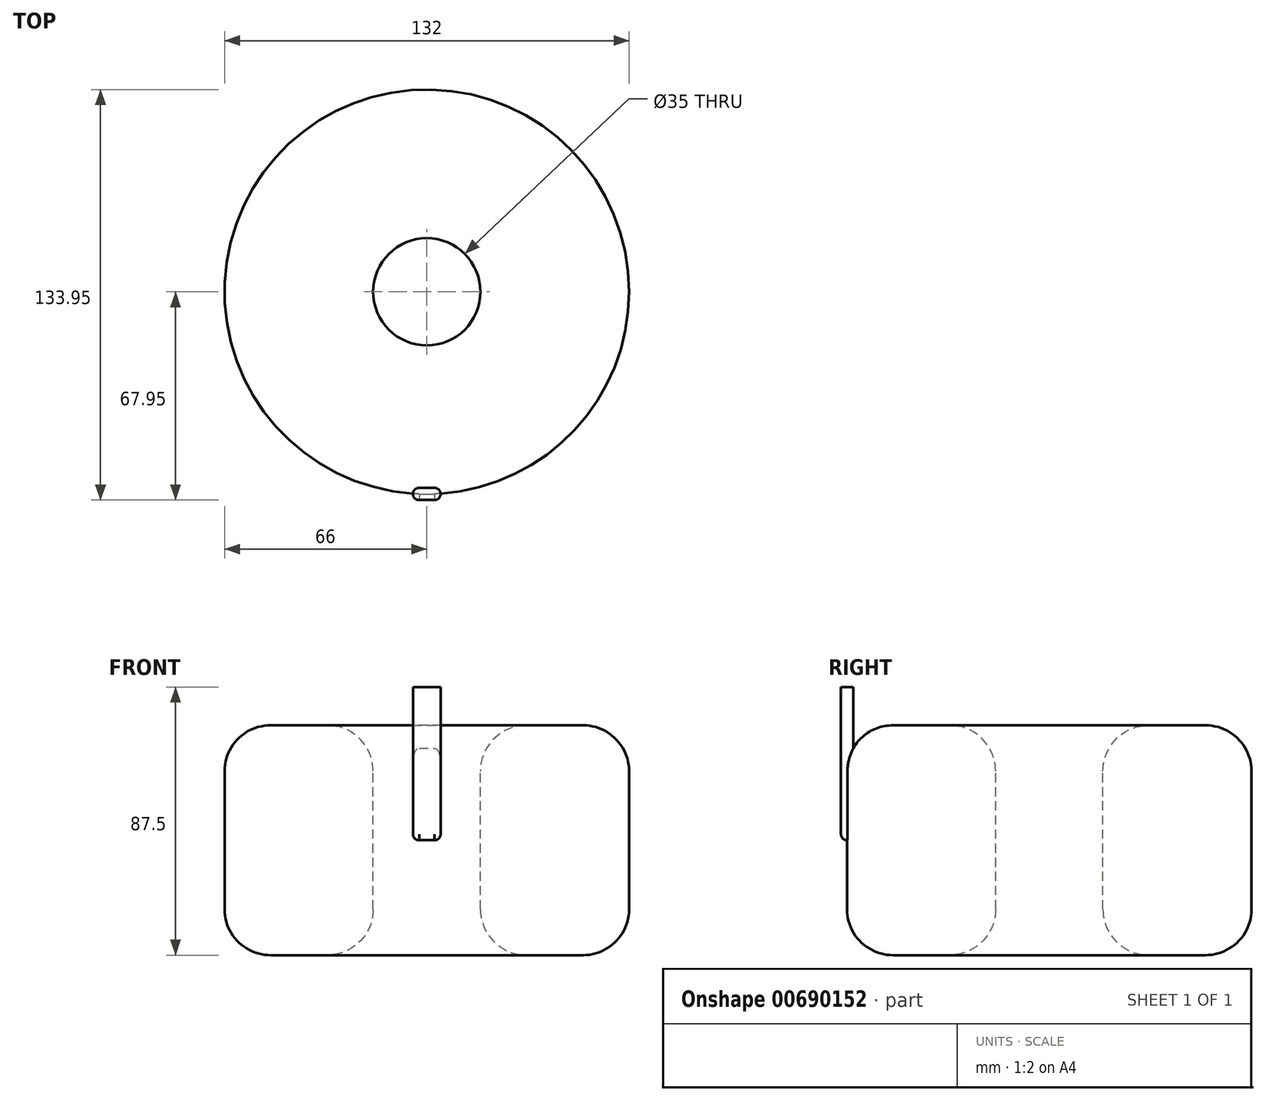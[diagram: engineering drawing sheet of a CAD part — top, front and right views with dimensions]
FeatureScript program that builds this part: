
annotation { "Feature Type Name" : "Feature", "Feature Type Description" : "" }
export const myFeature = defineFeature(function(context is Context, id is Id, definition is map)
    precondition{}
    {
        {
            var Q0;
            Q0=qCreatedBy(makeId("Top.planeOp"),FACE);
            var sketch = newSketch(context, id + "F0", { "sketchPlane" : qUnion([Q0])});
            skCircle(sketch, "E0", {"center": v(0, 0) * mm, "radius": 17.5 * mm});
            skCircle(sketch, "E1", {"center": v(0, 0) * mm, "radius": 66 * mm});
            skSolve(sketch);
        }
        {
            var Q0;
            Q0 = qSketchRegion(id + "F0", true);
            extrude(context, id + "F1", {"entities" : qUnion([Q0]), "endBound" : BoundingType.SYMMETRIC, "oppositeDirection" : true, "depth" : 75 * mm, "offsetDistance" : 25 * mm});
        }
        {
            var Q0;
            Q0=makeQuery(id+"F1.opExtrude","SWEPT_FACE",FACE,{"disambiguationData":[OSD([sQuery(id+"F0.wireOp",EDGE,"E0")])]});
            var Q1;
            Q1=makeQuery(id+"F1.opExtrude","SWEPT_FACE",FACE,{"disambiguationData":[OSD([sQuery(id+"F0.wireOp",EDGE,"E1")])]});
            fillet(context, id + "F2", {"entities" : qUnion([Q0, Q1]), "tangentPropagation" : true, "radius" : 15 * mm, "defaultsChanged" : true, "vertexSettings" : [], "allowEdgeOverflow" : false});
        }
        {
            var Q0;
            Q0=qCreatedBy(makeId("Top.planeOp"),FACE);
            var sketch = newSketch(context, id + "F3", { "sketchPlane" : qUnion([Q0])});
            skArc(sketch, "E2", {"start": v(-2.5, -63.95) * mm, "mid": v(-4.5, -65.95) * mm, "end": v(-2.5, -67.95) * mm});
            skLineSegment(sketch, "E3", {"start": v(2.5, -63.95) * mm, "end": v(-2.5, -63.95) * mm});
            skLineSegment(sketch, "E4", {"start": v(-2.5, -67.95) * mm, "end": v(2.5, -67.95) * mm});
            skArc(sketch, "E5.trimOffspring", {"start": v(2.5, -63.95) * mm, "mid": v(4.5, -65.95) * mm, "end": v(2.5, -67.95) * mm});
            skSolve(sketch);
        }
        {
            var Q0;
            Q0 = qSketchRegion(id + "F3", true);
            extrude(context, id + "F4", {"entities" : qUnion([Q0]), "operationType" : NewBodyOperationType.ADD, "depth" : 50 * mm, "offsetDistance" : 25 * mm});
        }
        {
            var Q0;
            Q0=makeQuery(id+"F4.opExtrude","CAP_EDGE",EDGE,{"disambiguationData":[OSD([sQuery(id+"F3.wireOp",EDGE,"E4")])],"isStart":true});
            fillet(context, id + "F5", {"entities" : qUnion([Q0]), "tangentPropagation" : true, "radius" : 2 * mm, "defaultsChanged" : true, "vertexSettings" : [], "allowEdgeOverflow" : false});
        }
    });
